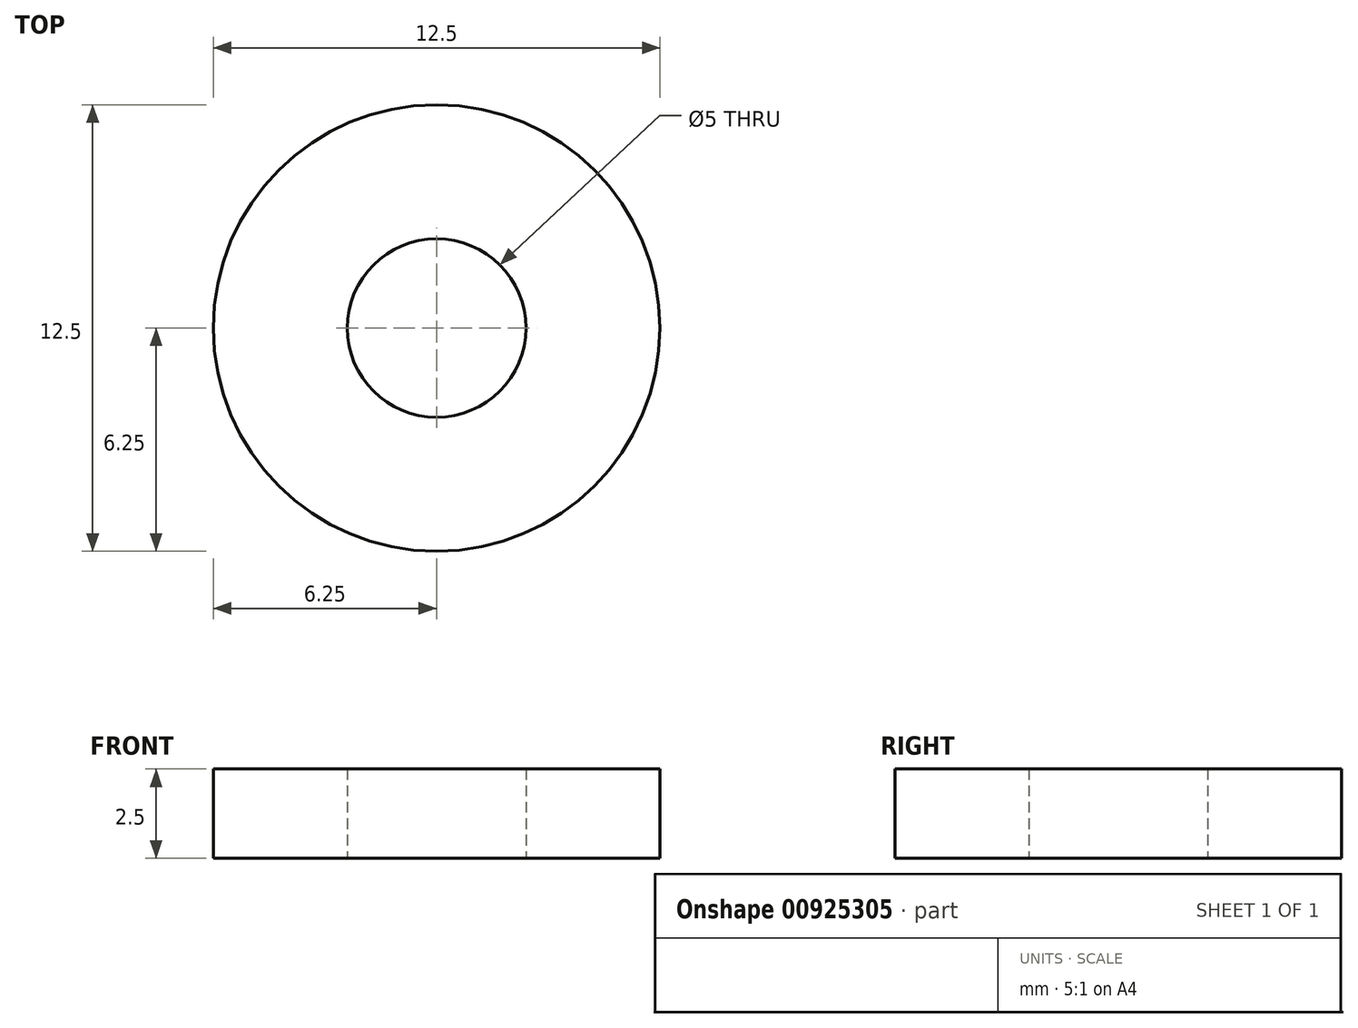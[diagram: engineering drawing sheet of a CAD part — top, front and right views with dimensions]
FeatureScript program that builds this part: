
annotation { "Feature Type Name" : "Feature", "Feature Type Description" : "" }
export const myFeature = defineFeature(function(context is Context, id is Id, definition is map)
    precondition{}
    {
        {
            var Q0;
            Q0=qCreatedBy(makeId("Top.planeOp"),FACE);
            var sketch = newSketch(context, id + "F0", { "sketchPlane" : qUnion([Q0])});
            skCircle(sketch, "E0", {"center": v(0, 0) * mm, "radius": 6.25 * mm});
            skCircle(sketch, "E1", {"center": v(0, 0) * mm, "radius": 2.5 * mm});
            skSolve(sketch);
        }
        {
            var Q0;
            Q0 = qSketchRegion(id + "F0", true);
            extrude(context, id + "F1", {"entities" : qUnion([Q0]), "depth" : 2.5 * mm, "offsetDistance" : 25.4 * mm});
        }
    });
